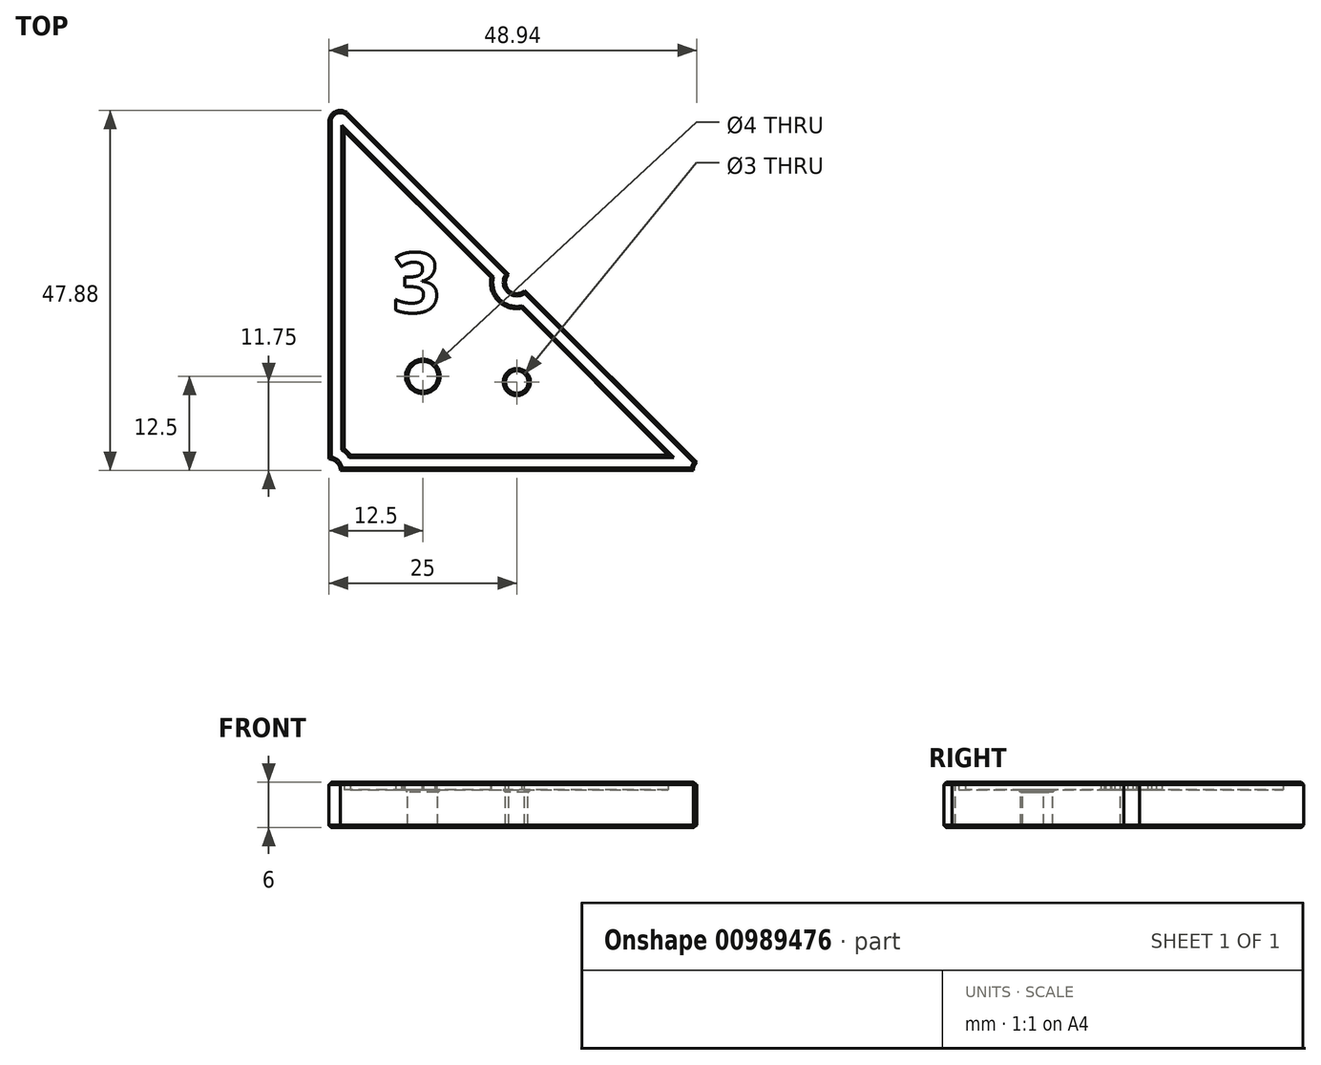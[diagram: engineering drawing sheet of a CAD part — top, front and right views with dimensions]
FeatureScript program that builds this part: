
annotation { "Feature Type Name" : "Feature", "Feature Type Description" : "" }
export const myFeature = defineFeature(function(context is Context, id is Id, definition is map)
    precondition{}
    {
        {
            var Q0;
            Q0=qCreatedBy(makeId("Top.planeOp"),FACE);
            var sketch = newSketch(context, id + "F0", { "sketchPlane" : qUnion([Q0])});
            skLineSegment(sketch, "E0", {"start": v(-25, 25) * mm, "end": v(-25, -25) * mm});
            skLineSegment(sketch, "E1", {"start": v(-25, -25) * mm, "end": v(25, -25) * mm});
            skLineSegment(sketch, "E2", {"start": v(25, -25) * mm, "end": v(-25, 25) * mm});
            skPoint(sketch, "E3", {"position": v(0, 0) * mm});
            skCircle(sketch, "E4", {"center": v(-25, -25) * mm, "radius": 1.5 * mm});
            skCircle(sketch, "E5", {"center": v(25, -25) * mm, "radius": 1.5 * mm});
            skCircle(sketch, "E6", {"center": v(0, 0) * mm, "radius": 1.5 * mm});
            skArc(sketch, "E7", {"start": v(-22.44, 22.44) * mm, "mid": v(-24.07, 22.76) * mm, "end": v(-25, 21.38) * mm});
            skCircle(sketch, "E8", {"center": v(-12.5, -12.5) * mm, "radius": 2 * mm});
            skLineSegment(sketch, "E9", {"start": v(0, 0) * mm, "end": v(-25, -25) * mm, "construction": true});
            skCircle(sketch, "E10", {"center": v(0, -13.25) * mm, "radius": 1.5 * mm});
            skLineSegment(sketch, "E11", {"start": v(0, -1.5) * mm, "end": v(0, -25) * mm, "construction": true});
            skPoint(sketch, "E11.startSnap0", {"position": v(0, -25) * mm});
            skLineSegment(sketch, "E12", {"start": v(-1.5, 1.5) * mm, "end": v(-1.5, -7.3) * mm, "construction": true});
            skLineSegment(sketch, "E13", {"start": v(-1.5, 0) * mm, "end": v(-25, 0) * mm, "construction": true});
            skText(sketch, "E14", { "text": "3", "fontName": "OpenSans-Bold.ttf"});
            skPoint(sketch, "E15", {"position": v(-13.25, 0) * mm});
            const initialGuessF0  = {"E14": [-0.01657, -0.004, 1, 0, 0.008]};
            skSetInitialGuess(sketch, initialGuessF0);
            skSolve(sketch);
        }
        {
            var Q0;
            Q0=makeQuery(id+"F0.imprint","IMPRINT",FACE,{"disambiguationData":[TD([[makeQuery(id+"F0.imprint","IMPRINT",EDGE,{"derivedFrom":sQuery(id+"F0.wireOp",EDGE,"E8")}),-1.0]])]});
            var Q1;
            Q1=makeQuery(id+"F0.imprint","IMPRINT",FACE,{"disambiguationData":[TD([[makeQuery(id+"F0.imprint","IMPRINT",EDGE,{"derivedFrom":sQuery(id+"F0.wireOp",EDGE,"E14.sketch_text.stroke-0")}),-1.0]])]});
            extrude(context, id + "F1", {"entities" : qUnion([Q0, Q1]), "oppositeDirection" : true, "depth" : 5 * mm, "offsetDistance" : 25 * mm});
        }
        {
            var Q0;
            Q0=makeQuery(id+"F1.opExtrude","CAP_FACE",FACE,{"disambiguationData":[OSD([sQuery(id+"F0.wireOp",EDGE,"E0"),sQuery(id+"F0.wireOp",EDGE,"E1"),sQuery(id+"F0.wireOp",EDGE,"E2"),sQuery(id+"F0.wireOp",EDGE,"E4"),sQuery(id+"F0.wireOp",EDGE,"E5"),sQuery(id+"F0.wireOp",EDGE,"E6"),sQuery(id+"F0.wireOp",EDGE,"E7"),sQuery(id+"F0.wireOp",EDGE,"E8"),sQuery(id+"F0.wireOp",EDGE,"E10")])],"isStart":true});
            var sketch = newSketch(context, id + "F2", { "sketchPlane" : qUnion([Q0])});
            skLineSegment(sketch, "E16.0", {"start": v(20.17, -23) * mm, "end": v(0.62, -3.45) * mm});
            skLineSegment(sketch, "E16.1", {"start": v(-3.45, 0.62) * mm, "end": v(-23, 20.17) * mm});
            skLineSegment(sketch, "E16.2", {"start": v(-23, 20.17) * mm, "end": v(-23, -22.13) * mm});
            skArc(sketch, "E16.3", {"start": v(0.62, -3.45) * mm, "mid": v(-2.47, -2.47) * mm, "end": v(-3.45, 0.62) * mm});
            skArc(sketch, "E16.4", {"start": v(-23, -22.13) * mm, "mid": v(-22.53, -22.53) * mm, "end": v(-22.13, -23) * mm});
            skLineSegment(sketch, "E16.5", {"start": v(-22.13, -23) * mm, "end": v(20.17, -23) * mm});
            skSolve(sketch);
        }
        {
            var Q0;
            Q0=makeQuery(id+"F0.imprint","IMPRINT",FACE,{"disambiguationData":[TD([[makeQuery(id+"F0.imprint","IMPRINT",EDGE,{"derivedFrom":sQuery(id+"F0.wireOp",EDGE,"E14.sketch_text.stroke-0")}),-1.0]])]});
            var Q1;
            Q1=makeQuery(id+"F2.imprint","IMPRINT",FACE,{"disambiguationData":[TD([[makeQuery(id+"F2.imprint","IMPRINT",EDGE,{"derivedFrom":sQuery(id+"F2.wireOp",EDGE,"E16.0")}),-1.0]])]});
            extrude(context, id + "F3", {"entities" : qUnion([Q0, Q1]), "operationType" : NewBodyOperationType.ADD, "depth" : 1 * mm, "offsetDistance" : 25 * mm});
        }
        {
            var Q0;
            Q0=makeQuery(id+"F3.opExtrude","CAP_FACE",FACE,{"disambiguationData":[OSD([sQuery(id+"F0.wireOp",EDGE,"E0"),sQuery(id+"F0.wireOp",EDGE,"E1"),sQuery(id+"F0.wireOp",EDGE,"E2"),sQuery(id+"F0.wireOp",EDGE,"E4"),sQuery(id+"F0.wireOp",EDGE,"E5"),sQuery(id+"F0.wireOp",EDGE,"E6"),sQuery(id+"F0.wireOp",EDGE,"E7"),sQuery(id+"F2.wireOp",EDGE,"E16.0"),sQuery(id+"F2.wireOp",EDGE,"E16.1"),sQuery(id+"F2.wireOp",EDGE,"E16.2"),sQuery(id+"F2.wireOp",EDGE,"E16.3"),sQuery(id+"F2.wireOp",EDGE,"E16.4"),sQuery(id+"F2.wireOp",EDGE,"E16.5")])],"isStart":false});
            var Q1;
            Q1=makeQuery(id+"F1.opExtrude","CAP_EDGE",EDGE,{"disambiguationData":[OSD([sQuery(id+"F0.wireOp",EDGE,"E8")])],"isStart":true});
            var Q2;
            Q2=makeQuery(id+"F1.opExtrude","CAP_EDGE",EDGE,{"disambiguationData":[OSD([sQuery(id+"F0.wireOp",EDGE,"E10")])],"isStart":true});
            var Q3;
            Q3=makeQuery(id+"F1.opExtrude","CAP_FACE",FACE,{"disambiguationData":[OSD([sQuery(id+"F0.wireOp",EDGE,"E0"),sQuery(id+"F0.wireOp",EDGE,"E1"),sQuery(id+"F0.wireOp",EDGE,"E2"),sQuery(id+"F0.wireOp",EDGE,"E4"),sQuery(id+"F0.wireOp",EDGE,"E5"),sQuery(id+"F0.wireOp",EDGE,"E6"),sQuery(id+"F0.wireOp",EDGE,"E7"),sQuery(id+"F0.wireOp",EDGE,"E8"),sQuery(id+"F0.wireOp",EDGE,"E10")])],"isStart":false});
            chamfer(context, id + "F4", {"entities" : qUnion([Q0, Q1, Q2, Q3]), "width" : 0.3 * mm, "tangentPropagation" : true});
        }
    });
